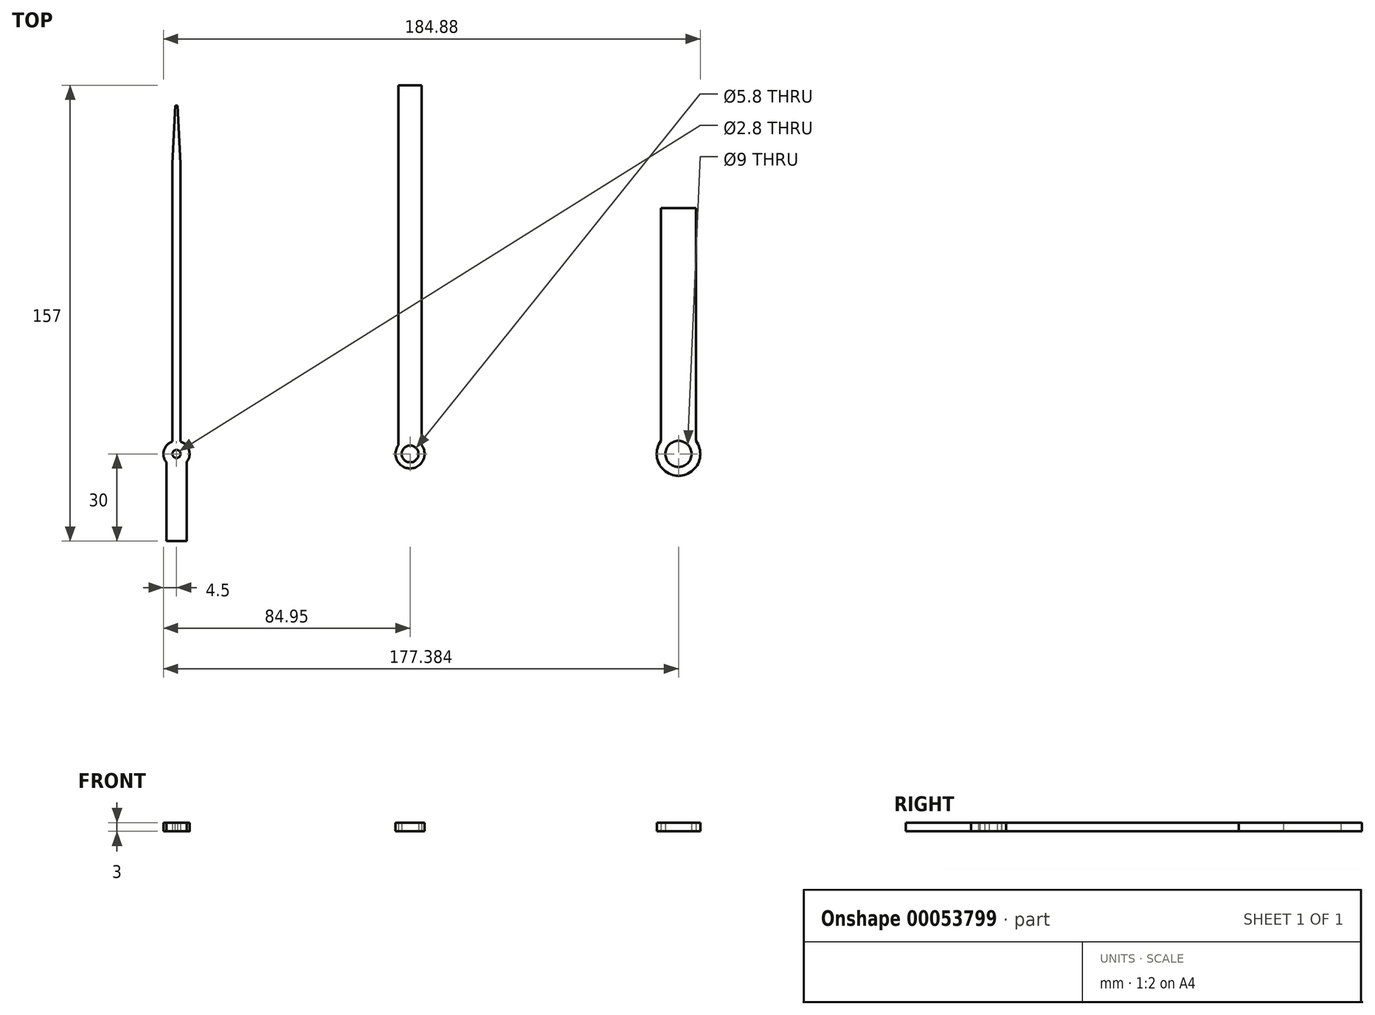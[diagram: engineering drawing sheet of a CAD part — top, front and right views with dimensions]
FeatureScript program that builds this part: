
annotation { "Feature Type Name" : "Feature", "Feature Type Description" : "" }
export const myFeature = defineFeature(function(context is Context, id is Id, definition is map)
    precondition{}
    {
        {
            var Q0;
            Q0=qCreatedBy(makeId("Top.planeOp"),FACE);
            var sketch = newSketch(context, id + "F0", { "sketchPlane" : qUnion([Q0])});
            skCircle(sketch, "E0", {"center": v(0, 0) * mm, "radius": 0.1 * mm});
            skCircle(sketch, "E1", {"center": v(0, 0) * mm, "radius": 4 * mm});
            skLineSegment(sketch, "E2", {"start": v(-165.51, 0) * mm, "end": v(180.55, 0) * mm, "construction": true});
            skLineSegment(sketch, "E3", {"start": v(0, -7.67) * mm, "end": v(0, 31.67) * mm, "construction": true});
            skCircle(sketch, "E4", {"center": v(0, 0) * mm, "radius": 5 * mm});
            skLineSegment(sketch, "E5", {"start": v(-81.85, 0) * mm, "end": v(-81.85, 120) * mm});
            skLineSegment(sketch, "E6", {"start": v(-79.05, 120) * mm, "end": v(-79.05, 0) * mm});
            skLineSegment(sketch, "E7.left", {"start": v(-83.95, 0) * mm, "end": v(-83.95, -30) * mm});
            skLineSegment(sketch, "E7.right", {"start": v(-76.95, 0) * mm, "end": v(-76.95, -30) * mm});
            skCircle(sketch, "E8", {"center": v(-80.45, 0) * mm, "radius": 4.5 * mm});
            skLineSegment(sketch, "E9", {"start": v(-80.45, -7.67) * mm, "end": v(-80.45, 31.67) * mm, "construction": true});
            skLineSegment(sketch, "E10", {"start": v(-81.85, 120) * mm, "end": v(-79.05, 120) * mm});
            skLineSegment(sketch, "E7.top", {"start": v(-83.95, -30) * mm, "end": v(-76.95, -30) * mm});
            skCircle(sketch, "E11", {"center": v(-80.45, 0) * mm, "radius": 3.5 * mm});
            skLineSegment(sketch, "E7.bottom", {"start": v(-83.95, 0) * mm, "end": v(-76.95, 0) * mm});
            skCircle(sketch, "E12", {"center": v(-80.45, 0) * mm, "radius": 1.4 * mm});
            skCircle(sketch, "E13", {"center": v(92.43, 0) * mm, "radius": 7.5 * mm});
            skLineSegment(sketch, "E14", {"start": v(92.43, -7.67) * mm, "end": v(92.43, 31.67) * mm, "construction": true});
            skCircle(sketch, "E15", {"center": v(92.43, 0) * mm, "radius": 6 * mm});
            skCircle(sketch, "E16", {"center": v(92.43, 0) * mm, "radius": 4.5 * mm});
            skCircle(sketch, "E17", {"center": v(0, 0) * mm, "radius": 2.9 * mm});
            skLineSegment(sketch, "E18", {"start": v(-4, 0) * mm, "end": v(-4, 127) * mm});
            skLineSegment(sketch, "E19", {"start": v(4, 0) * mm, "end": v(4, 127) * mm});
            skLineSegment(sketch, "E20", {"start": v(-4, 127) * mm, "end": v(4, 127) * mm});
            skLineSegment(sketch, "E21", {"start": v(86.43, 0) * mm, "end": v(86.43, 84.67) * mm});
            skLineSegment(sketch, "E22", {"start": v(86.43, 84.67) * mm, "end": v(98.43, 84.67) * mm});
            skLineSegment(sketch, "E23", {"start": v(98.43, 0) * mm, "end": v(98.43, 84.67) * mm});
            skSolve(sketch);
        }
        {
            var Q0;
            {var subQ0=sQuery(id+"F0.wireOp",EDGE,"E10");Q0=makeQuery(id+"F0.imprint","IMPRINT",FACE,{"disambiguationData":[TD([[makeQuery(id+"F0.imprint","IMPRINT",EDGE,{"derivedFrom":subQ0}),-1.0]])]});}
            var Q1;
            {var subQ0=sQuery(id+"F0.wireOp",EDGE,"E7.top");Q1=makeQuery(id+"F0.imprint","IMPRINT",FACE,{"disambiguationData":[TD([[makeQuery(id+"F0.imprint","IMPRINT",EDGE,{"derivedFrom":subQ0}),1.0]])]});}
            var Q2;
            {var subQ2=sQuery(id+"F0.wireOp",EDGE,"E7.left");var subQ4=sQuery(id+"F0.wireOp",EDGE,"E8");var subQ5=makeQuery(id+"F0.imprint","INTERSECT",VERTEX,{"derivedFrom":[subQ2,subQ4]});Q2=makeQuery(id+"F0.imprint","IMPRINT",FACE,{"disambiguationData":[TD([[makeQuery(id+"F0.imprint","IMPRINT",EDGE,{"disambiguationData":[TD([[subQ5,-1.0]])],"derivedFrom":subQ4}),1.0]])]});}
            var Q3;
            {var subQ0=sQuery(id+"F0.wireOp",EDGE,"E8");var subQ1=sQuery(id+"F0.wireOp",EDGE,"E6");var subQ2=makeQuery(id+"F0.imprint","INTERSECT",VERTEX,{"derivedFrom":[subQ1,subQ0]});Q3=makeQuery(id+"F0.imprint","IMPRINT",FACE,{"disambiguationData":[TD([[makeQuery(id+"F0.imprint","IMPRINT",EDGE,{"disambiguationData":[TD([[subQ2,-1.0]])],"derivedFrom":subQ1}),1.0]])]});}
            var Q4;
            {var subQ0=sQuery(id+"F0.wireOp",EDGE,"E7.bottom");var subQ1=sQuery(id+"F0.wireOp",EDGE,"E11");var subQ2=makeQuery(id+"F0.imprint","INTERSECT",VERTEX,{"derivedFrom":[sQuery(id+"F0.wireOp",EDGE,"E7.left"),subQ1,subQ0]});Q4=makeQuery(id+"F0.imprint","IMPRINT",FACE,{"disambiguationData":[TD([[makeQuery(id+"F0.imprint","IMPRINT",EDGE,{"disambiguationData":[TD([[subQ2,-1.0]])],"derivedFrom":subQ1}),1.0]])]});}
            var Q5;
            {var subQ0=sQuery(id+"F0.wireOp",EDGE,"E8");var subQ1=sQuery(id+"F0.wireOp",EDGE,"E5");var subQ2=makeQuery(id+"F0.imprint","INTERSECT",VERTEX,{"derivedFrom":[subQ1,subQ0]});Q5=makeQuery(id+"F0.imprint","IMPRINT",FACE,{"disambiguationData":[TD([[makeQuery(id+"F0.imprint","IMPRINT",EDGE,{"disambiguationData":[TD([[subQ2,1.0]])],"derivedFrom":subQ1}),1.0]])]});}
            var Q6;
            {var subQ0=sQuery(id+"F0.wireOp",EDGE,"E8");var subQ1=sQuery(id+"F0.wireOp",EDGE,"E5");var subQ2=makeQuery(id+"F0.imprint","INTERSECT",VERTEX,{"derivedFrom":[subQ1,subQ0]});Q6=makeQuery(id+"F0.imprint","IMPRINT",FACE,{"disambiguationData":[TD([[makeQuery(id+"F0.imprint","IMPRINT",EDGE,{"disambiguationData":[TD([[subQ2,1.0]])],"derivedFrom":subQ1}),-1.0]])]});}
            var Q7;
            {var subQ2=sQuery(id+"F0.wireOp",EDGE,"E5");var subQ4=sQuery(id+"F0.wireOp",EDGE,"E11");var subQ5=makeQuery(id+"F0.imprint","INTERSECT",VERTEX,{"derivedFrom":[subQ2,subQ4]});Q7=makeQuery(id+"F0.imprint","IMPRINT",FACE,{"disambiguationData":[TD([[makeQuery(id+"F0.imprint","IMPRINT",EDGE,{"disambiguationData":[TD([[subQ5,1.0]])],"derivedFrom":subQ4}),1.0]])]});}
            var Q8;
            {var subQ1=sQuery(id+"F0.wireOp",EDGE,"E6");var subQ3=sQuery(id+"F0.wireOp",EDGE,"E11");var subQ4=makeQuery(id+"F0.imprint","INTERSECT",VERTEX,{"derivedFrom":[subQ1,subQ3]});Q8=makeQuery(id+"F0.imprint","IMPRINT",FACE,{"disambiguationData":[TD([[makeQuery(id+"F0.imprint","IMPRINT",EDGE,{"disambiguationData":[TD([[subQ4,-1.0]])],"derivedFrom":subQ1}),1.0]])]});}
            var Q9;
            {var subQ1=sQuery(id+"F0.wireOp",EDGE,"E5");var subQ3=sQuery(id+"F0.wireOp",EDGE,"E11");var subQ4=makeQuery(id+"F0.imprint","INTERSECT",VERTEX,{"derivedFrom":[subQ1,subQ3]});Q9=makeQuery(id+"F0.imprint","IMPRINT",FACE,{"disambiguationData":[TD([[makeQuery(id+"F0.imprint","IMPRINT",EDGE,{"disambiguationData":[TD([[subQ4,1.0]])],"derivedFrom":subQ1}),1.0]])]});}
            var Q10;
            {var subQ0=sQuery(id+"F0.wireOp",EDGE,"E18");var subQ1=sQuery(id+"F0.wireOp",EDGE,"E1");var subQ2=makeQuery(id+"F0.imprint","INTERSECT",VERTEX,{"derivedFrom":[subQ1,subQ0]});Q10=makeQuery(id+"F0.imprint","IMPRINT",FACE,{"disambiguationData":[TD([[makeQuery(id+"F0.imprint","IMPRINT",EDGE,{"disambiguationData":[TD([[subQ2,-1.0]])],"derivedFrom":subQ1}),-1.0]])]});}
            var Q11;
            Q11=makeQuery(id+"F0.imprint","IMPRINT",FACE,{"disambiguationData":[TD([[makeQuery(id+"F0.imprint","IMPRINT",EDGE,{"derivedFrom":sQuery(id+"F0.wireOp",EDGE,"E17")}),-1.0]])]});
            var Q12;
            {var subQ0=sQuery(id+"F0.wireOp",EDGE,"E18");var subQ1=sQuery(id+"F0.wireOp",EDGE,"E1");var subQ2=makeQuery(id+"F0.imprint","INTERSECT",VERTEX,{"derivedFrom":[subQ1,subQ0]});Q12=makeQuery(id+"F0.imprint","IMPRINT",FACE,{"disambiguationData":[TD([[makeQuery(id+"F0.imprint","IMPRINT",EDGE,{"disambiguationData":[TD([[subQ2,1.0]])],"derivedFrom":subQ1}),-1.0]])]});}
            var Q13;
            {var subQ5=sQuery(id+"F0.wireOp",EDGE,"E20");Q13=makeQuery(id+"F0.imprint","IMPRINT",FACE,{"disambiguationData":[TD([[makeQuery(id+"F0.imprint","IMPRINT",EDGE,{"derivedFrom":subQ5}),-1.0]])]});}
            var Q14;
            {var subQ5=sQuery(id+"F0.wireOp",EDGE,"E22");Q14=makeQuery(id+"F0.imprint","IMPRINT",FACE,{"disambiguationData":[TD([[makeQuery(id+"F0.imprint","IMPRINT",EDGE,{"derivedFrom":subQ5}),-1.0]])]});}
            var Q15;
            {var subQ0=sQuery(id+"F0.wireOp",EDGE,"E21");var subQ1=sQuery(id+"F0.wireOp",EDGE,"E13");var subQ2=makeQuery(id+"F0.imprint","INTERSECT",VERTEX,{"derivedFrom":[subQ1,subQ0]});Q15=makeQuery(id+"F0.imprint","IMPRINT",FACE,{"disambiguationData":[TD([[makeQuery(id+"F0.imprint","IMPRINT",EDGE,{"disambiguationData":[TD([[subQ2,1.0]])],"derivedFrom":subQ1}),1.0]])]});}
            var Q16;
            Q16=makeQuery(id+"F0.imprint","IMPRINT",FACE,{"disambiguationData":[TD([[makeQuery(id+"F0.imprint","IMPRINT",EDGE,{"derivedFrom":sQuery(id+"F0.wireOp",EDGE,"E16")}),-1.0]])]});
            var Q17;
            {var subQ0=sQuery(id+"F0.wireOp",EDGE,"E21");var subQ1=sQuery(id+"F0.wireOp",EDGE,"E13");var subQ2=makeQuery(id+"F0.imprint","INTERSECT",VERTEX,{"derivedFrom":[subQ1,subQ0]});Q17=makeQuery(id+"F0.imprint","IMPRINT",FACE,{"disambiguationData":[TD([[makeQuery(id+"F0.imprint","IMPRINT",EDGE,{"disambiguationData":[TD([[subQ2,-1.0]])],"derivedFrom":subQ1}),1.0]])]});}
            extrude(context, id + "F1", {"entities" : qUnion([Q0, Q1, Q2, Q3, Q4, Q5, Q6, Q7, Q8, Q9, Q10, Q11, Q12, Q13, Q14, Q15, Q16, Q17]), "depth" : 3 * mm});
        }
        {
            var Q0;
            Q0=makeQuery(id+"F1.opExtrude","SWEPT_EDGE",EDGE,{"disambiguationData":[OSD([sQuery(id+"F0.wireOp",EDGE,"E6"),sQuery(id+"F0.wireOp",EDGE,"E10")])]});
            var Q1;
            Q1=makeQuery(id+"F1.opExtrude","SWEPT_EDGE",EDGE,{"disambiguationData":[OSD([sQuery(id+"F0.wireOp",EDGE,"E5"),sQuery(id+"F0.wireOp",EDGE,"E10")])]});
            chamfer(context, id + "F2", {"entities" : qUnion([Q0, Q1]), "chamferType" : ChamferType.TWO_OFFSETS, "width1" : 1 * mm, "oppositeDirection" : false, "width2" : 20 * mm, "tangentPropagation" : true});
        }
    });
